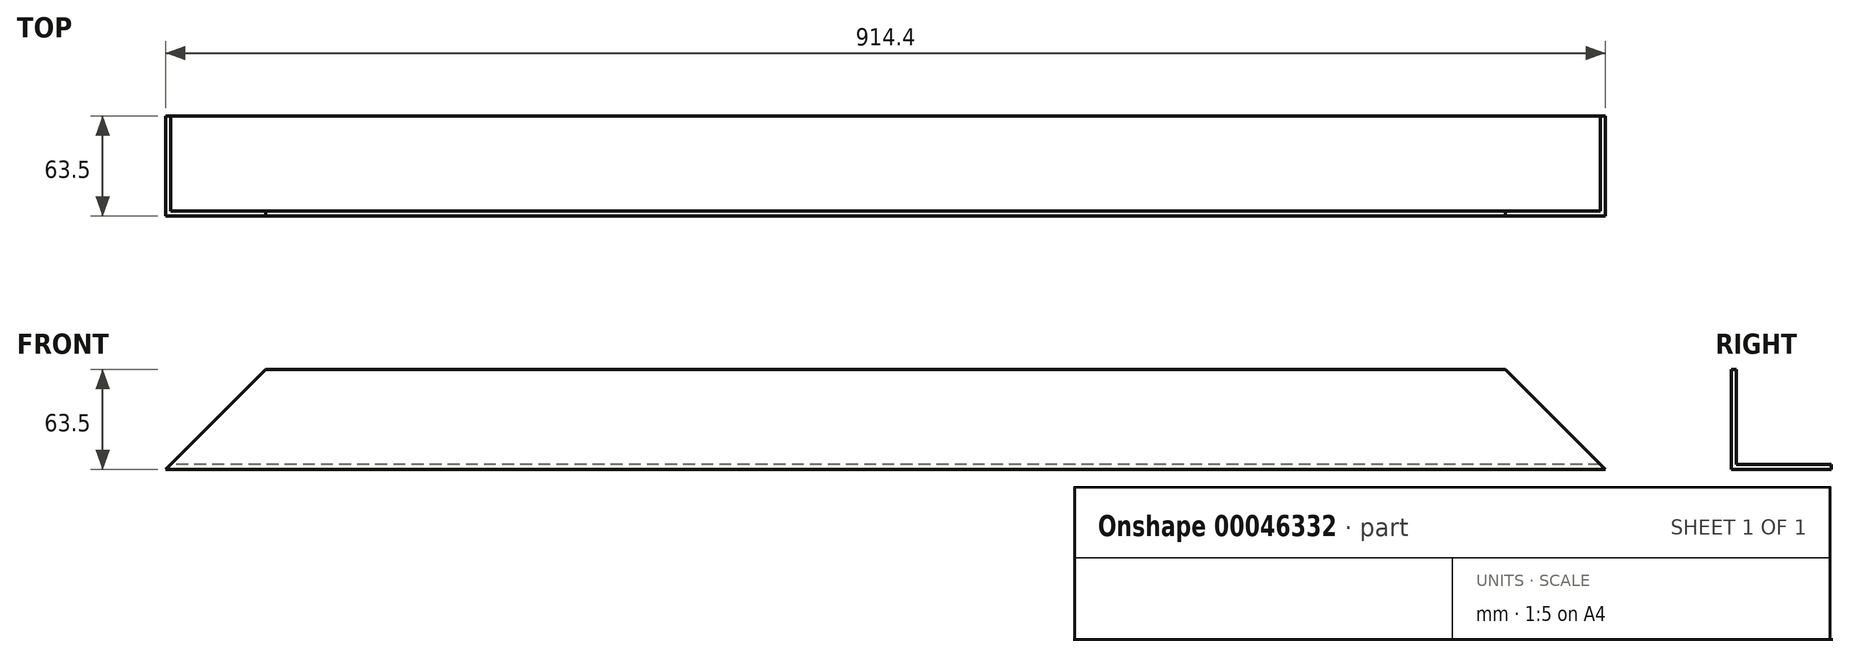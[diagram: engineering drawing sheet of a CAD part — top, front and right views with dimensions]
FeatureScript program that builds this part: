
annotation { "Feature Type Name" : "Feature", "Feature Type Description" : "" }
export const myFeature = defineFeature(function(context is Context, id is Id, definition is map)
    precondition{}
    {
        {
            var Q0;
            Q0=qCreatedBy(makeId("Right.planeOp"),FACE);
            var sketch = newSketch(context, id + "F0", { "sketchPlane" : qUnion([Q0])});
            skLineSegment(sketch, "E0", {"start": v(0, 0) * mm, "end": v(63.5, 0) * mm});
            skLineSegment(sketch, "E1", {"start": v(63.5, 0) * mm, "end": v(63.5, 3.18) * mm});
            skLineSegment(sketch, "E2", {"start": v(63.5, 3.18) * mm, "end": v(3.18, 3.17) * mm});
            skLineSegment(sketch, "E3", {"start": v(3.18, 3.18) * mm, "end": v(3.18, 63.5) * mm});
            skLineSegment(sketch, "E4", {"start": v(3.18, 63.5) * mm, "end": v(0, 63.5) * mm});
            skLineSegment(sketch, "E5", {"start": v(0, 63.5) * mm, "end": v(0, 0) * mm});
            skSolve(sketch);
        }
        {
            var Q0;
            Q0=makeQuery(id+"F0.imprint","IMPRINT",FACE,{"disambiguationData":[TD([[makeQuery(id+"F0.imprint","IMPRINT",EDGE,{"derivedFrom":sQuery(id+"F0.wireOp",EDGE,"E0")}),1.0]])]});
            extrude(context, id + "F1", {"entities" : qUnion([Q0]), "endBound" : BoundingType.SYMMETRIC, "depth" : 914.4 * mm});
        }
        {
            var Q0;
            Q0=makeQuery(id+"F1.opExtrude","SWEPT_FACE",FACE,{"disambiguationData":[OSD([sQuery(id+"F0.wireOp",EDGE,"E5")])]});
            var sketch = newSketch(context, id + "F2", { "sketchPlane" : qUnion([Q0])});
            skLineSegment(sketch, "E6", {"start": v(-457.2, 0) * mm, "end": v(457.2, 0) * mm});
            skLineSegment(sketch, "E7", {"start": v(457.2, 0) * mm, "end": v(360.84, 96.36) * mm});
            skLineSegment(sketch, "E8", {"start": v(360.84, 96.36) * mm, "end": v(-360.84, 96.36) * mm});
            skLineSegment(sketch, "E9", {"start": v(-360.84, 96.36) * mm, "end": v(-457.2, 0) * mm});
            skSolve(sketch);
        }
        {
            var Q0;
            {var subQ0=sQuery(id+"F0.wireOp",EDGE,"E5");var subQ4=makeQuery(id+"F1.opExtrude","CAP_EDGE",EDGE,{"disambiguationData":[OSD([subQ0])],"isStart":true});Q0=makeQuery(id+"F2.imprint","IMPRINT",FACE,{"disambiguationData":[TD([[makeQuery(id+"F2.imprint","IMPRINT",EDGE,{"derivedFrom":subQ4}),1.0]])]});}
            var Q1;
            {var subQ0=sQuery(id+"F0.wireOp",EDGE,"E5");var subQ1=makeQuery(id+"F1.opExtrude","CAP_EDGE",EDGE,{"disambiguationData":[OSD([subQ0])],"isStart":false});Q1=makeQuery(id+"F2.imprint","IMPRINT",FACE,{"disambiguationData":[TD([[makeQuery(id+"F2.imprint","IMPRINT",EDGE,{"derivedFrom":subQ1}),-1.0]])]});}
            extrude(context, id + "F3", {"entities" : qUnion([Q0, Q1]), "operationType" : NewBodyOperationType.REMOVE, "oppositeDirection" : true, "depth" : 76.2 * mm});
        }
    });
